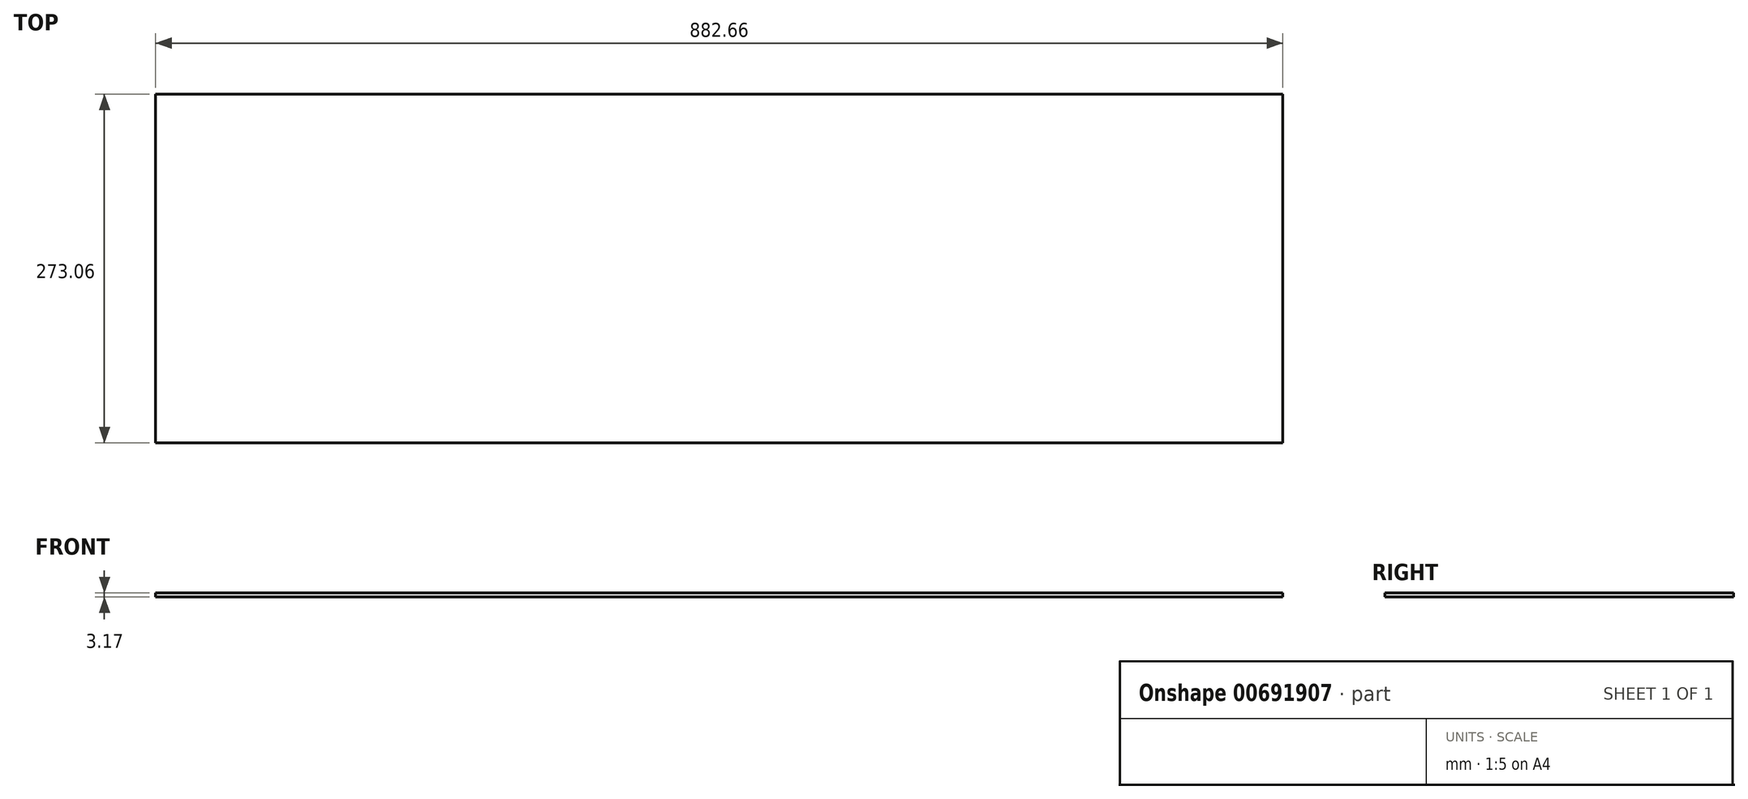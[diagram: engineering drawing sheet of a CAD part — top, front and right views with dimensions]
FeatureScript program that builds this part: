
annotation { "Feature Type Name" : "Feature", "Feature Type Description" : "" }
export const myFeature = defineFeature(function(context is Context, id is Id, definition is map)
    precondition{}
    {
        {
            var Q0;
            Q0=qCreatedBy(makeId("Top.planeOp"),FACE);
            var sketch = newSketch(context, id + "F0", { "sketchPlane" : qUnion([Q0])});
            skLineSegment(sketch, "E0.bottom", {"start": v(441.33, -136.53) * mm, "end": v(-441.33, -136.53) * mm});
            skLineSegment(sketch, "E0.top", {"start": v(441.33, 136.53) * mm, "end": v(-441.33, 136.53) * mm});
            skLineSegment(sketch, "E0.left", {"start": v(441.33, -136.53) * mm, "end": v(441.33, 136.53) * mm});
            skLineSegment(sketch, "E0.right", {"start": v(-441.33, -136.53) * mm, "end": v(-441.33, 136.52) * mm});
            skPoint(sketch, "E0.middle", {"position": v(0, 0) * mm});
            skSolve(sketch);
        }
        {
            var Q0;
            Q0=makeQuery(id+"F0.imprint","IMPRINT",FACE,{"disambiguationData":[TD([[makeQuery(id+"F0.imprint","IMPRINT",EDGE,{"derivedFrom":sQuery(id+"F0.wireOp",EDGE,"E0.bottom")}),-1.0]])]});
            extrude(context, id + "F1", {"entities" : qUnion([Q0]), "depth" : 3.17 * mm, "offsetDistance" : 25.4 * mm});
        }
    });
